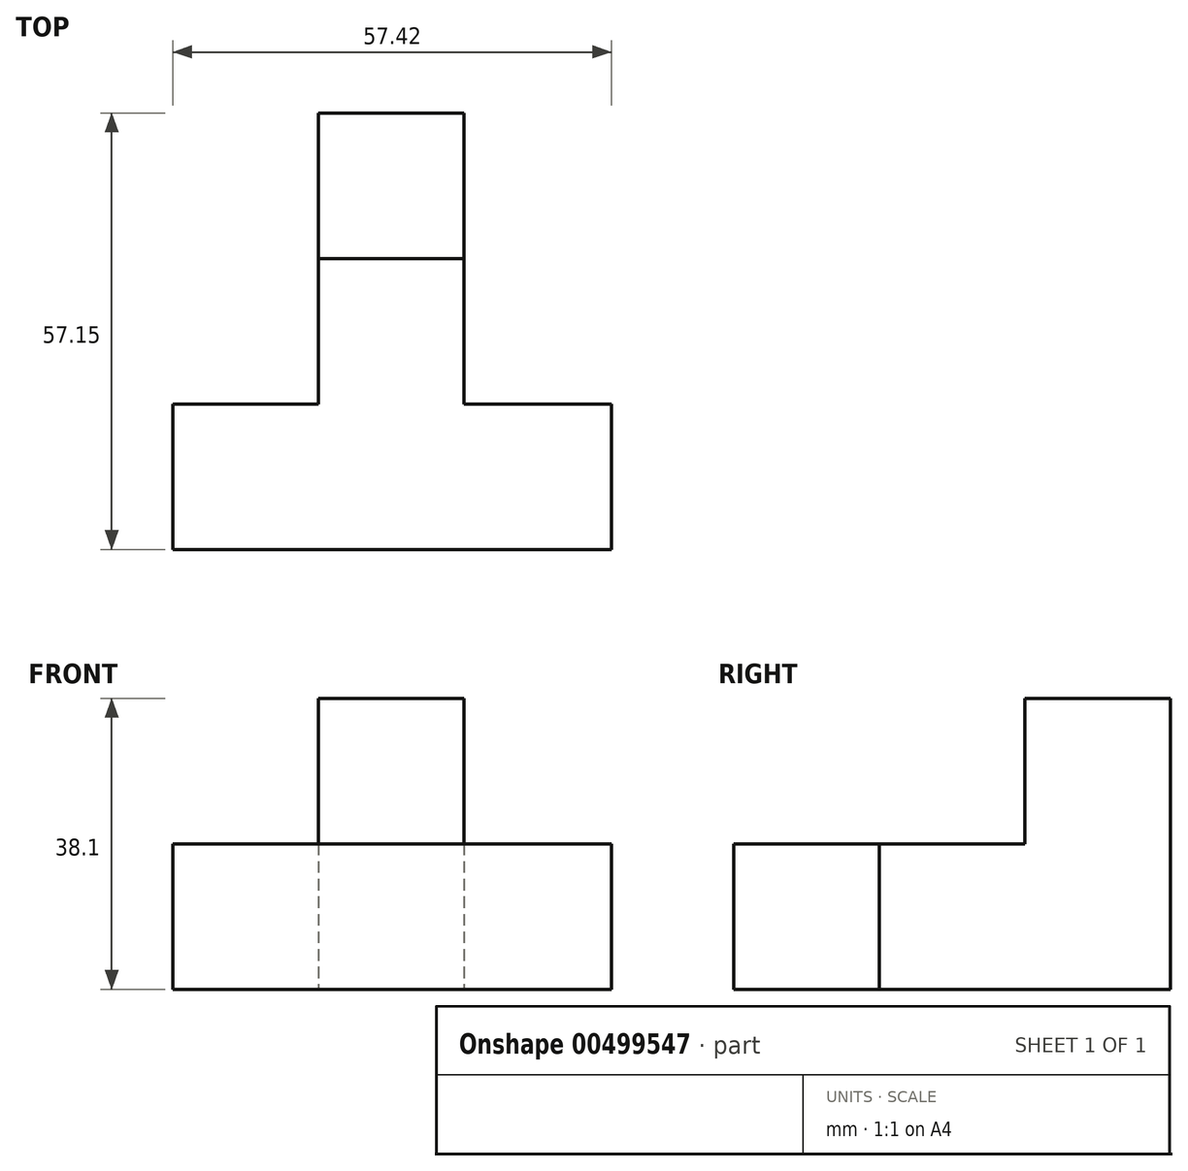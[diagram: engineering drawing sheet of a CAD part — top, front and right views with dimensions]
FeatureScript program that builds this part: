
annotation { "Feature Type Name" : "Feature", "Feature Type Description" : "" }
export const myFeature = defineFeature(function(context is Context, id is Id, definition is map)
    precondition{}
    {
        {
            var Q0;
            Q0=qCreatedBy(makeId("Top.planeOp"),FACE);
            var sketch = newSketch(context, id + "F0", { "sketchPlane" : qUnion([Q0])});
            skLineSegment(sketch, "E0.bottom", {"start": v(0, 0) * mm, "end": v(-19.05, 0) * mm});
            skLineSegment(sketch, "E0.top", {"start": v(0, 19.05) * mm, "end": v(-19.05, 19.05) * mm});
            skLineSegment(sketch, "E0.left", {"start": v(0, 0) * mm, "end": v(0, 19.05) * mm});
            skLineSegment(sketch, "E0.right", {"start": v(-19.05, 0) * mm, "end": v(-19.05, 19.05) * mm});
            skLineSegment(sketch, "E1.bottom", {"start": v(-19.05, 19.05) * mm, "end": v(0, 19.05) * mm});
            skLineSegment(sketch, "E1.top", {"start": v(-19.05, 38.1) * mm, "end": v(0, 38.1) * mm});
            skLineSegment(sketch, "E1.left", {"start": v(-19.05, 19.05) * mm, "end": v(-19.05, 38.1) * mm});
            skLineSegment(sketch, "E1.right", {"start": v(0, 19.05) * mm, "end": v(0, 38.1) * mm});
            skLineSegment(sketch, "E2.bottom", {"start": v(0, 0) * mm, "end": v(19.32, 0) * mm});
            skLineSegment(sketch, "E2.top", {"start": v(0, 19.05) * mm, "end": v(19.32, 19.05) * mm});
            skLineSegment(sketch, "E2.right", {"start": v(19.32, 0) * mm, "end": v(19.32, 19.05) * mm});
            skLineSegment(sketch, "E3.bottom", {"start": v(-19.05, 0) * mm, "end": v(-38.1, 0) * mm});
            skLineSegment(sketch, "E3.top", {"start": v(-19.05, 19.05) * mm, "end": v(-38.1, 19.05) * mm});
            skLineSegment(sketch, "E3.right", {"start": v(-38.1, 0) * mm, "end": v(-38.1, 19.05) * mm});
            skLineSegment(sketch, "E4.top", {"start": v(-19.05, 57.15) * mm, "end": v(0, 57.15) * mm});
            skLineSegment(sketch, "E4.left", {"start": v(-19.05, 38.1) * mm, "end": v(-19.05, 57.15) * mm});
            skLineSegment(sketch, "E4.right", {"start": v(0, 38.1) * mm, "end": v(0, 57.15) * mm});
            skSolve(sketch);
        }
        {
            var Q0;
            Q0 = qSketchRegion(id + "F0", true);
            extrude(context, id + "F1", {"entities" : qUnion([Q0]), "depth" : 19.05 * mm});
        }
        {
            var Q0;
            Q0=makeQuery(id+"F0.imprint","IMPRINT",FACE,{"disambiguationData":[TD([[makeQuery(id+"F0.imprint","IMPRINT",EDGE,{"derivedFrom":sQuery(id+"F0.wireOp",EDGE,"E1.top")}),1.0]])]});
            extrude(context, id + "F2", {"entities" : qUnion([Q0]), "operationType" : NewBodyOperationType.ADD, "depth" : 38.1 * mm});
        }
    });
